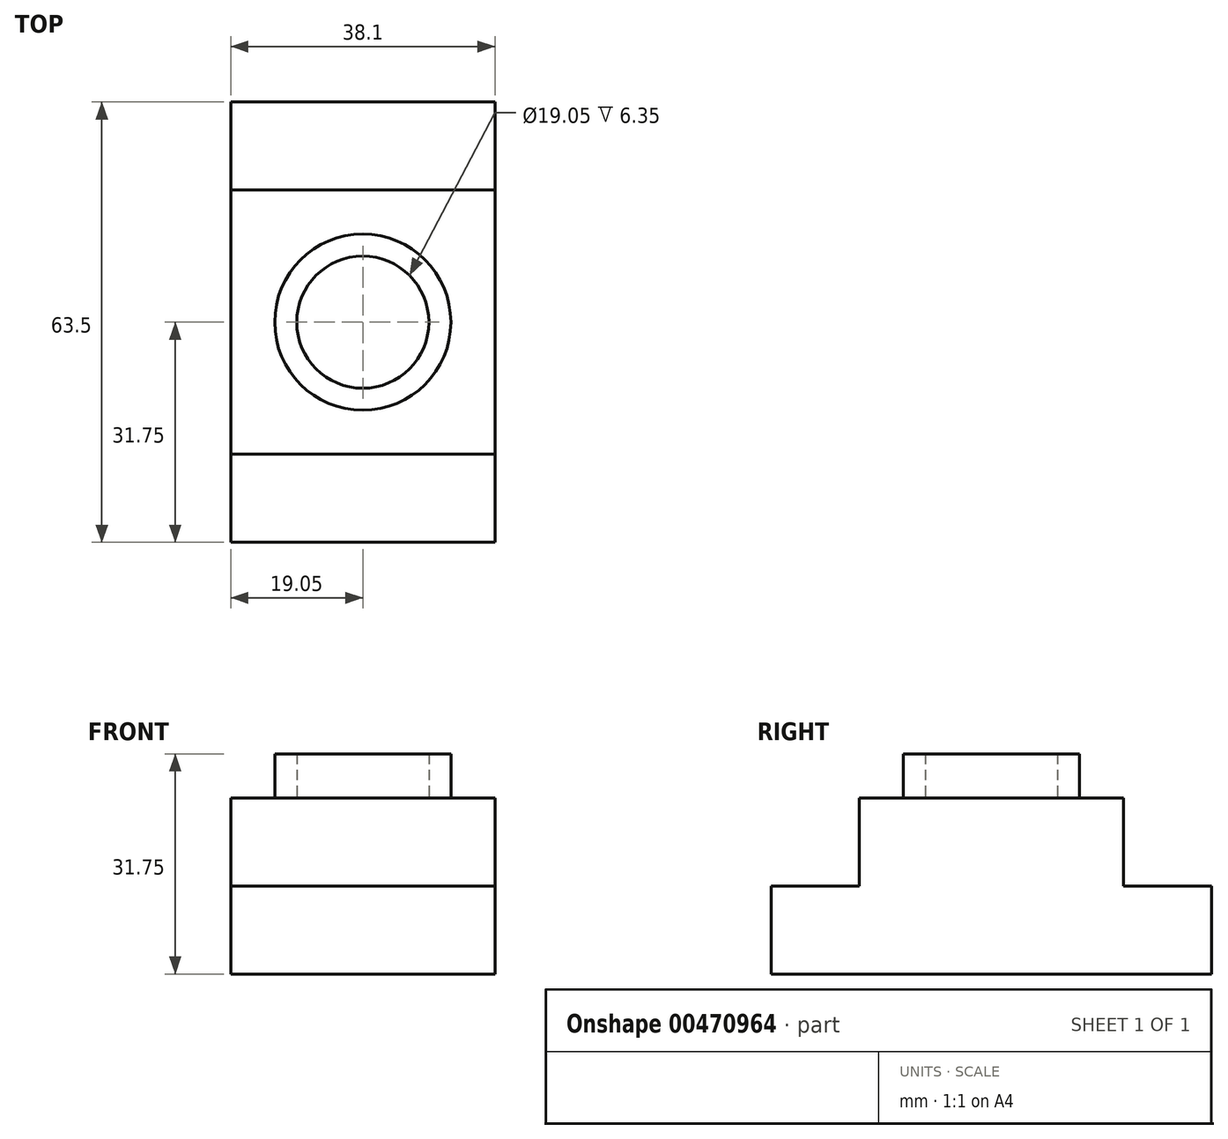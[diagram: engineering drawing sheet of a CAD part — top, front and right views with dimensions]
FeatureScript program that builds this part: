
annotation { "Feature Type Name" : "Feature", "Feature Type Description" : "" }
export const myFeature = defineFeature(function(context is Context, id is Id, definition is map)
    precondition{}
    {
        {
            var Q0;
            Q0=qCreatedBy(makeId("Right.planeOp"),FACE);
            var sketch = newSketch(context, id + "F0", { "sketchPlane" : qUnion([Q0])});
            skLineSegment(sketch, "E0", {"start": v(0, 0) * mm, "end": v(-31.75, 0) * mm});
            skLineSegment(sketch, "E1", {"start": v(-31.75, 0) * mm, "end": v(-31.75, 12.7) * mm});
            skLineSegment(sketch, "E2", {"start": v(-31.75, 12.7) * mm, "end": v(-19.05, 12.7) * mm});
            skLineSegment(sketch, "E3", {"start": v(-19.05, 12.7) * mm, "end": v(-19.05, 25.4) * mm});
            skLineSegment(sketch, "E4", {"start": v(-19.05, 25.4) * mm, "end": v(19.05, 25.4) * mm});
            skLineSegment(sketch, "E5", {"start": v(19.05, 25.4) * mm, "end": v(19.05, 12.7) * mm});
            skLineSegment(sketch, "E6", {"start": v(19.05, 12.7) * mm, "end": v(31.75, 12.7) * mm});
            skLineSegment(sketch, "E7", {"start": v(31.75, 12.7) * mm, "end": v(31.75, 0) * mm});
            skLineSegment(sketch, "E8", {"start": v(31.75, 0) * mm, "end": v(0, 0) * mm});
            skSolve(sketch);
        }
        {
            var Q0;
            Q0 = qSketchRegion(id + "F0", true);
            extrude(context, id + "F1", {"entities" : qUnion([Q0]), "depth" : 38.1 * mm});
        }
        {
            var Q0;
            Q0=makeQuery(id+"F1.opExtrude","SWEPT_FACE",FACE,{"disambiguationData":[OSD([sQuery(id+"F0.wireOp",EDGE,"E4")])]});
            var sketch = newSketch(context, id + "F2", { "sketchPlane" : qUnion([Q0])});
            skCircle(sketch, "E9", {"center": v(19.05, 0) * mm, "radius": 12.7 * mm});
            skCircle(sketch, "E10", {"center": v(19.05, 0) * mm, "radius": 9.53 * mm});
            skSolve(sketch);
        }
        {
            var Q0;
            Q0 = qSketchRegion(id + "FSXgGKU4ao11ZCq_1", true);
            var Q1;
            Q1=makeQuery(id+"F2.imprint","IMPRINT",FACE,{"disambiguationData":[TD([[makeQuery(id+"F2.imprint","IMPRINT",EDGE,{"derivedFrom":sQuery(id+"F2.wireOp",EDGE,"E9")}),1.0]])]});
            extrude(context, id + "F3", {"entities" : qUnion([Q0, Q1]), "operationType" : NewBodyOperationType.ADD, "depth" : 6.35 * mm});
        }
    });
